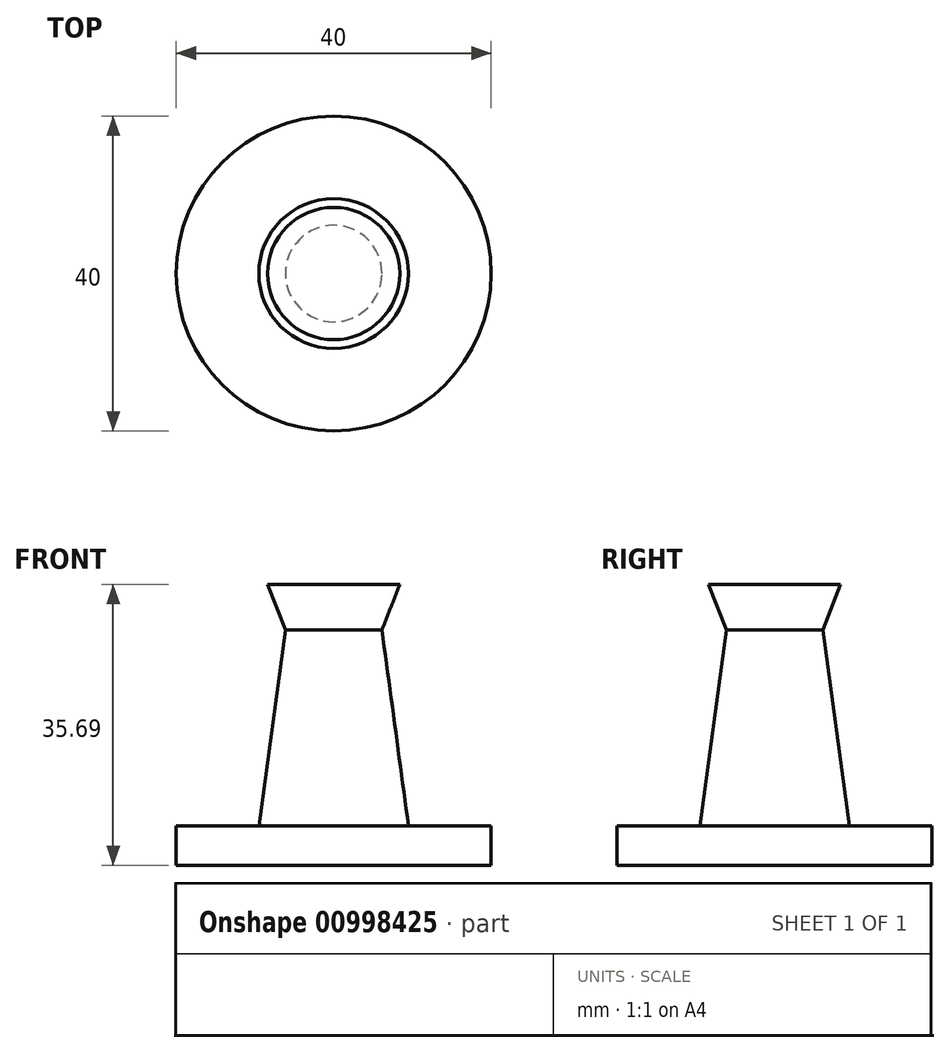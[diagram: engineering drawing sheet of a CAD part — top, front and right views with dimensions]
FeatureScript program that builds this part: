
annotation { "Feature Type Name" : "Feature", "Feature Type Description" : "" }
export const myFeature = defineFeature(function(context is Context, id is Id, definition is map)
    precondition{}
    {
        {
            var Q0;
            Q0=qCreatedBy(makeId("Front.planeOp"),FACE);
            var sketch = newSketch(context, id + "F0", { "sketchPlane" : qUnion([Q0])});
            skLineSegment(sketch, "E0", {"start": v(0, 0) * mm, "end": v(20, 0) * mm});
            skLineSegment(sketch, "E1", {"start": v(20, 0) * mm, "end": v(20, 5) * mm});
            skLineSegment(sketch, "E2", {"start": v(20, 5) * mm, "end": v(9.5, 5) * mm});
            skLineSegment(sketch, "E3", {"start": v(9.5, 5) * mm, "end": v(6.13, 29.92) * mm});
            skLineSegment(sketch, "E4", {"start": v(6.13, 29.92) * mm, "end": v(8.4, 35.69) * mm});
            skLineSegment(sketch, "E5", {"start": v(0, 35.69) * mm, "end": v(8.4, 35.69) * mm});
            skLineSegment(sketch, "E6", {"start": v(0, 35.69) * mm, "end": v(0, 0) * mm});
            skSolve(sketch);
        }
        {
            var Q0;
            Q0 = qSketchRegion(id + "F0", true);
            var Q1;
            Q1=sQuery(id+"F0.wireOp",EDGE,"E6");
            revolve(context, id + "F1", {"surfaceOperationType" : NewSurfaceOperationType.NEW, "entities" : qUnion([Q0]), "axis" : qUnion([Q1]), "revolveType" : RevolveType.FULL});
        }
    });
